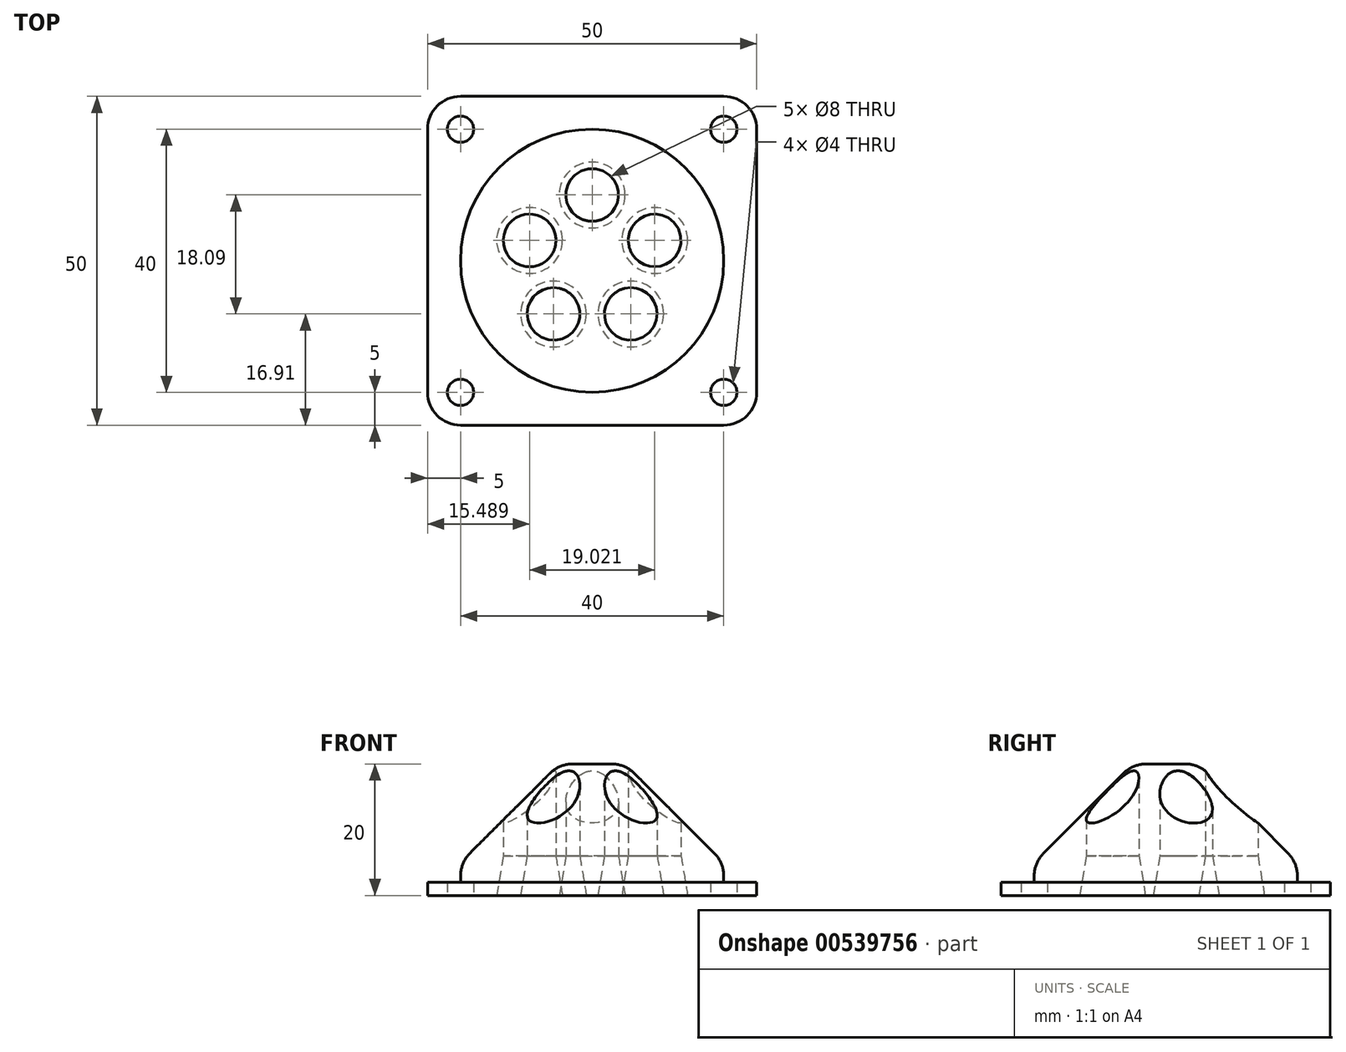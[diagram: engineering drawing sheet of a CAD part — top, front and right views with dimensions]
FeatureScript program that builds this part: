
annotation { "Feature Type Name" : "Feature", "Feature Type Description" : "" }
export const myFeature = defineFeature(function(context is Context, id is Id, definition is map)
    precondition{}
    {
        {
            var Q0;
            Q0=qCreatedBy(makeId("Top.planeOp"),FACE);
            var sketch = newSketch(context, id + "F0", { "sketchPlane" : qUnion([Q0])});
            skCircle(sketch, "E0", {"center": v(0, 0) * mm, "radius": 20 * mm});
            skCircle(sketch, "E1", {"center": v(0, 10) * mm, "radius": 4 * mm});
            skCircle(sketch, "E2.1.0", {"center": v(-9.51, 3.1) * mm, "radius": 4 * mm});
            skCircle(sketch, "E2.2.0", {"center": v(-5.88, -8.1) * mm, "radius": 4 * mm});
            skCircle(sketch, "E2.3.0", {"center": v(5.88, -8.1) * mm, "radius": 4 * mm});
            skCircle(sketch, "E2.4.0", {"center": v(9.51, 3.1) * mm, "radius": 4 * mm});
            skLineSegment(sketch, "E3.bottom", {"start": v(25, -25) * mm, "end": v(-25, -25) * mm});
            skLineSegment(sketch, "E3.top", {"start": v(25, 25) * mm, "end": v(-25, 25) * mm});
            skLineSegment(sketch, "E3.left", {"start": v(25, -25) * mm, "end": v(25, 25) * mm});
            skLineSegment(sketch, "E3.right", {"start": v(-25, -25) * mm, "end": v(-25, 25) * mm});
            skPoint(sketch, "E4", {"position": v(-20, 20) * mm});
            skPoint(sketch, "E5.MirrorP", {"position": v(20, 20) * mm});
            skPoint(sketch, "E6.MirrorP", {"position": v(-20, -20) * mm});
            skPoint(sketch, "E7.MirrorP", {"position": v(20, -20) * mm});
            skSolve(sketch);
        }
        {
            var Q0;
            Q0=makeQuery(id+"F0.imprint","IMPRINT",FACE,{"disambiguationData":[TD([[makeQuery(id+"F0.imprint","IMPRINT",EDGE,{"derivedFrom":sQuery(id+"F0.wireOp",EDGE,"E0")}),1.0]])]});
            extrude(context, id + "F1", {"entities" : qUnion([Q0]), "depth" : 20 * mm, "offsetDistance" : 25 * mm});
        }
        {
            var Q0;
            Q0=makeQuery(id+"F1.opExtrude","CAP_EDGE",EDGE,{"disambiguationData":[OSD([sQuery(id+"F0.wireOp",EDGE,"E0")])],"isStart":false});
            chamfer(context, id + "F2", {"entities" : qUnion([Q0]), "width" : 15 * mm, "tangentPropagation" : true});
        }
        {
            var Q0;
            Q0=makeQuery(id+"F0.imprint","IMPRINT",FACE,{"disambiguationData":[TD([[makeQuery(id+"F0.imprint","IMPRINT",EDGE,{"derivedFrom":sQuery(id+"F0.wireOp",EDGE,"E0")}),-1.0]])]});
            extrude(context, id + "F3", {"entities" : qUnion([Q0]), "operationType" : NewBodyOperationType.ADD, "depth" : 2 * mm, "offsetDistance" : 25 * mm});
        }
        {
            var Q0;
            Q0=makeQuery(id+"F3.opExtrude","SWEPT_EDGE",EDGE,{"disambiguationData":[OSD([sQuery(id+"F0.wireOp",EDGE,"E3.top"),sQuery(id+"F0.wireOp",EDGE,"E3.right")])]});
            var Q1;
            Q1=makeQuery(id+"F3.opExtrude","SWEPT_EDGE",EDGE,{"disambiguationData":[OSD([sQuery(id+"F0.wireOp",EDGE,"E3.top"),sQuery(id+"F0.wireOp",EDGE,"E3.left")])]});
            var Q2;
            Q2=makeQuery(id+"F3.opExtrude","SWEPT_EDGE",EDGE,{"disambiguationData":[OSD([sQuery(id+"F0.wireOp",EDGE,"E3.bottom"),sQuery(id+"F0.wireOp",EDGE,"E3.left")])]});
            var Q3;
            Q3=makeQuery(id+"F3.opExtrude","SWEPT_EDGE",EDGE,{"disambiguationData":[OSD([sQuery(id+"F0.wireOp",EDGE,"E3.bottom"),sQuery(id+"F0.wireOp",EDGE,"E3.right")])]});
            fillet(context, id + "F4", {"entities" : qUnion([Q0, Q1, Q2, Q3]), "radius" : 5 * mm, "tangentPropagation" : true, "allowEdgeOverflow" : false});
        }
        {
            var Q0;
            Q0=sQuery(id+"F0.wireOp",VERTEX,"E4");
            var Q1;
            Q1=sQuery(id+"F0.wireOp",VERTEX,"E5.MirrorP");
            var Q2;
            Q2=sQuery(id+"F0.wireOp",VERTEX,"E7.MirrorP");
            var Q3;
            Q3=sQuery(id+"F0.wireOp",VERTEX,"E6.MirrorP");
            var Q4;
            Q4=makeQuery(id+"F1.opExtrude","SWEPT_BODY",BODY,{"disambiguationData":[OSD([sQuery(id+"F0.wireOp",EDGE,"E0"),sQuery(id+"F0.wireOp",EDGE,"E1"),sQuery(id+"F0.wireOp",EDGE,"E2.1.0"),sQuery(id+"F0.wireOp",EDGE,"E2.2.0"),sQuery(id+"F0.wireOp",EDGE,"E2.3.0"),sQuery(id+"F0.wireOp",EDGE,"E2.4.0")])]});
            hole(context, id + "F5", {"style" : HoleStyle.SIMPLE, "endStyle" : HoleEndStyle.THROUGH, "oppositeDirection" : true, "holeDiameter" : 4 * mm, "majorDiameter" : 5 * mm, "isTappedThrough" : true, "tappedDepth" : 12 * mm, "tapClearance" : 3, "locations" : qUnion([Q0, Q1, Q2, Q3]), "scope" : qUnion([Q4])});
        }
        {
            var Q0;
            Q0=makeQuery(id+"F1.opExtrude","CAP_FACE",FACE,{"disambiguationData":[OSD([sQuery(id+"F0.wireOp",EDGE,"E0"),sQuery(id+"F0.wireOp",EDGE,"E1"),sQuery(id+"F0.wireOp",EDGE,"E2.1.0"),sQuery(id+"F0.wireOp",EDGE,"E2.2.0"),sQuery(id+"F0.wireOp",EDGE,"E2.3.0"),sQuery(id+"F0.wireOp",EDGE,"E2.4.0")])],"isStart":false});
            fillet(context, id + "F6", {"entities" : qUnion([Q0]), "radius" : 5 * mm, "tangentPropagation" : true, "allowEdgeOverflow" : false});
        }
        {
            var Q0;
            Q0=makeQuery(id+"F1.opExtrude","CAP_EDGE",EDGE,{"disambiguationData":[OSD([sQuery(id+"F0.wireOp",EDGE,"E2.4.0")])],"isStart":true});
            var Q1;
            Q1=makeQuery(id+"F1.opExtrude","CAP_EDGE",EDGE,{"disambiguationData":[OSD([sQuery(id+"F0.wireOp",EDGE,"E1")])],"isStart":true});
            var Q2;
            Q2=makeQuery(id+"F1.opExtrude","CAP_EDGE",EDGE,{"disambiguationData":[OSD([sQuery(id+"F0.wireOp",EDGE,"E2.1.0")])],"isStart":true});
            var Q3;
            Q3=makeQuery(id+"F1.opExtrude","CAP_EDGE",EDGE,{"disambiguationData":[OSD([sQuery(id+"F0.wireOp",EDGE,"E2.2.0")])],"isStart":true});
            var Q4;
            Q4=makeQuery(id+"F1.opExtrude","CAP_EDGE",EDGE,{"disambiguationData":[OSD([sQuery(id+"F0.wireOp",EDGE,"E2.3.0")])],"isStart":true});
            chamfer(context, id + "F7", {"entities" : qUnion([Q0, Q1, Q2, Q3, Q4]), "chamferType" : ChamferType.TWO_OFFSETS, "width1" : 1 * mm, "oppositeDirection" : false, "width2" : 6 * mm, "tangentPropagation" : true});
        }
        {
            var Q0;
            {var subQ0=sQuery(id+"F0.wireOp",EDGE,"E0");Q0=makeQuery(id+"F2.opChamfer","BLEND_EDGE",EDGE,{"blendedFrom":[makeQuery(id+"F1.opExtrude","CAP_EDGE",EDGE,{"disambiguationData":[OSD([subQ0])],"isStart":false}),makeQuery(id+"F1.opExtrude","SWEPT_FACE",FACE,{"disambiguationData":[OSD([subQ0])]})],"blendedInto":[makeQuery(id+"F1.opExtrude","SWEPT_FACE",FACE,{"disambiguationData":[OSD([subQ0])]})]});}
            fillet(context, id + "F8", {"entities" : qUnion([Q0]), "radius" : 5 * mm, "tangentPropagation" : true, "allowEdgeOverflow" : false});
        }
    });
